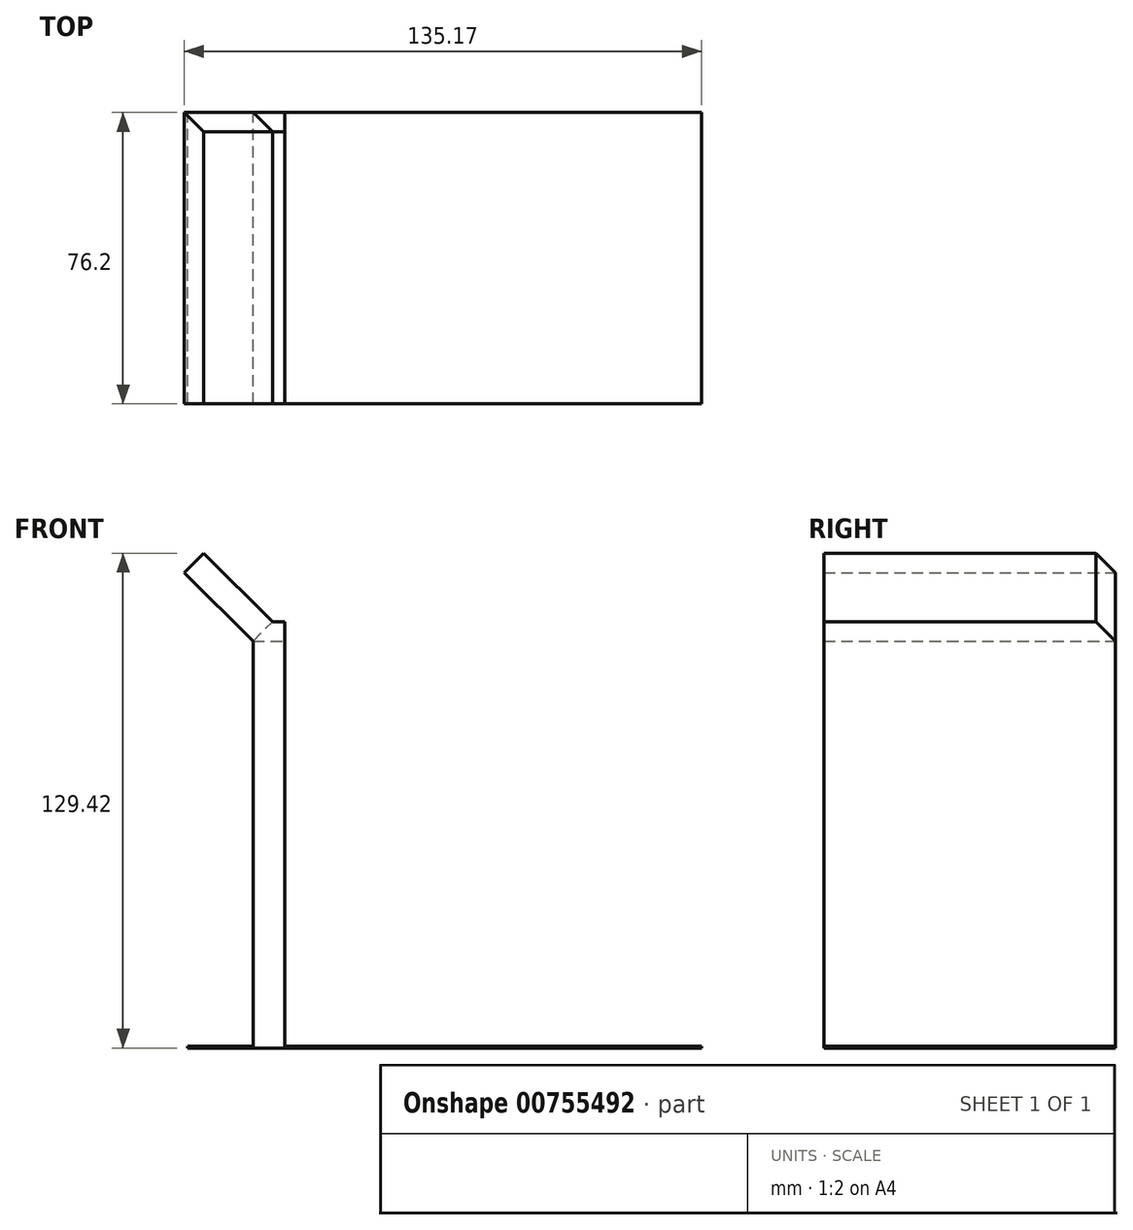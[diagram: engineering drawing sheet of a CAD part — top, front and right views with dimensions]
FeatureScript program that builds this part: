
annotation { "Feature Type Name" : "Feature", "Feature Type Description" : "" }
export const myFeature = defineFeature(function(context is Context, id is Id, definition is map)
    precondition{}
    {
        {
            var Q0;
            Q0=qCreatedBy(makeId("Front.planeOp"),FACE);
            var sketch = newSketch(context, id + "F0", { "sketchPlane" : qUnion([Q0])});
            skLineSegment(sketch, "E0.bottom", {"start": v(-68.32, 60.66) * mm, "end": v(-76.66, 60.66) * mm});
            skLineSegment(sketch, "E0.top", {"start": v(-68.32, -50.4) * mm, "end": v(-76.66, -50.4) * mm});
            skLineSegment(sketch, "E0.left", {"start": v(-68.32, 60.66) * mm, "end": v(-68.32, -50.4) * mm});
            skLineSegment(sketch, "E0.right", {"start": v(-76.66, 60.66) * mm, "end": v(-76.66, -50.4) * mm});
            skLineSegment(sketch, "E1.bottom", {"start": v(-68.32, -50.4) * mm, "end": v(40.55, -50.4) * mm});
            skLineSegment(sketch, "E1.top", {"start": v(-68.32, -50.8) * mm, "end": v(40.55, -50.8) * mm});
            skLineSegment(sketch, "E1.left", {"start": v(-68.32, -50.8) * mm, "end": v(-68.32, -50.4) * mm});
            skLineSegment(sketch, "E1.right", {"start": v(40.55, -50.8) * mm, "end": v(40.55, -50.4) * mm});
            skSolve(sketch);
        }
        {
            var Q0;
            Q0 = qSketchRegion(id + "F0", true);
            extrude(context, id + "F1", {"entities" : qUnion([Q0]), "depth" : 76.2 * mm, "offsetDistance" : 25.4 * mm});
        }
        {
            var Q0;
            Q0=makeQuery(id+"F1.opExtrude","SWEPT_FACE",FACE,{"disambiguationData":[OSD([sQuery(id+"F0.wireOp",EDGE,"E1.left")])]});
            extrude(context, id + "F2", {"entities" : qUnion([Q0]), "operationType" : NewBodyOperationType.ADD, "depth" : 25.4 * mm, "offsetDistance" : 25.4 * mm});
        }
        {
            var Q0;
            Q0=makeQuery(id+"F1.opExtrude","SWEPT_EDGE",EDGE,{"disambiguationData":[OSD([sQuery(id+"F0.wireOp",EDGE,"E0.bottom"),sQuery(id+"F0.wireOp",EDGE,"E0.right")])]});
            var Q1;
            Q1=makeQuery(id+"F1.opExtrude","CAP_EDGE",EDGE,{"disambiguationData":[OSD([sQuery(id+"F0.wireOp",EDGE,"E0.bottom")])],"isStart":true});
            chamfer(context, id + "F3", {"entities" : qUnion([Q0, Q1]), "width" : 5.08 * mm, "tangentPropagation" : true});
        }
        {
            var Q0;
            Q0=makeQuery(id+"F3.opChamfer","BLEND_FACE",FACE,{"disambiguationData":[OSD([sQuery(id+"F0.wireOp",EDGE,"E0.bottom"),sQuery(id+"F0.wireOp",EDGE,"E0.right")])]});
            extrude(context, id + "F4", {"entities" : qUnion([Q0]), "operationType" : NewBodyOperationType.ADD, "depth" : 25.4 * mm, "offsetDistance" : 25.4 * mm});
        }
    });
